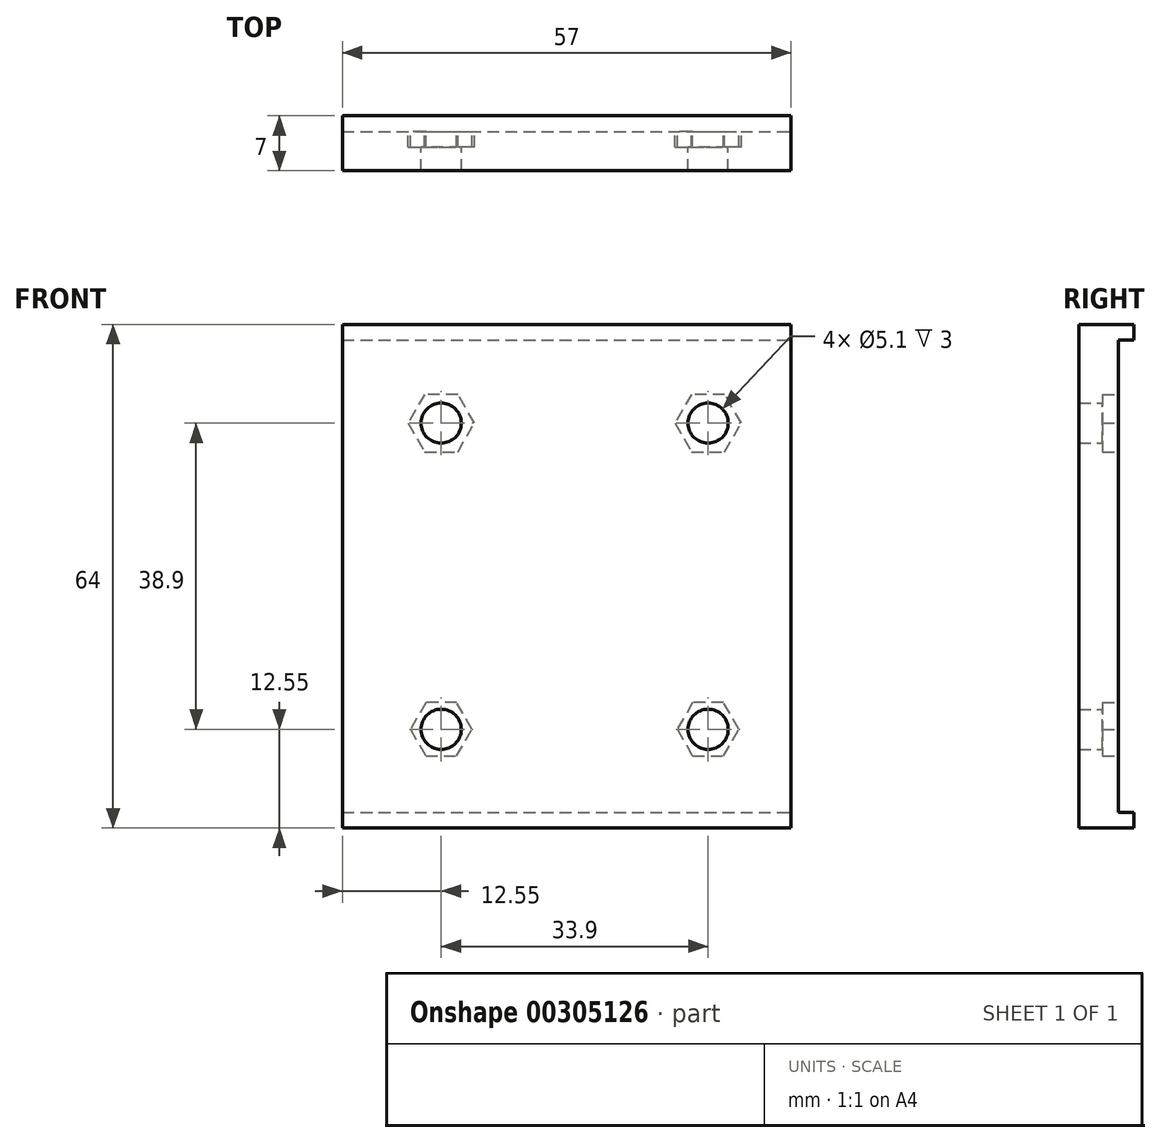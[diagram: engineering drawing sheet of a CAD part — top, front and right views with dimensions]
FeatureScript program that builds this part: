
annotation { "Feature Type Name" : "Feature", "Feature Type Description" : "" }
export const myFeature = defineFeature(function(context is Context, id is Id, definition is map)
    precondition{}
    {
        {
            var Q0;
            Q0=qCreatedBy(makeId("Front.planeOp"),FACE);
            var sketch = newSketch(context, id + "F0", { "sketchPlane" : qUnion([Q0])});
            skLineSegment(sketch, "E0.left", {"start": v(-55, 58.9) * mm, "end": v(-55, -1.1) * mm});
            skLineSegment(sketch, "E0.right", {"start": v(2, 58.9) * mm, "end": v(2, -1.1) * mm});
            skLineSegment(sketch, "E1.0", {"start": v(-55, 58.9) * mm, "end": v(2, 58.9) * mm});
            skLineSegment(sketch, "E2.0", {"start": v(-55, -1.1) * mm, "end": v(2, -1.1) * mm});
            skCircle(sketch, "E3", {"center": v(-42.45, 48.35) * mm, "radius": 2.55 * mm});
            skCircle(sketch, "E4", {"center": v(-8.55, 48.35) * mm, "radius": 2.55 * mm});
            skCircle(sketch, "E5", {"center": v(-42.45, 9.45) * mm, "radius": 2.55 * mm});
            skCircle(sketch, "E6", {"center": v(-8.55, 9.45) * mm, "radius": 2.55 * mm});
            skSolve(sketch);
        }
        {
            var Q0;
            {var subQ0=sQuery(id+"F0.wireOp",EDGE,"E1.0");Q0=makeQuery(id+"F0.imprint","IMPRINT",FACE,{"disambiguationData":[TD([[makeQuery(id+"F0.imprint","IMPRINT",EDGE,{"derivedFrom":subQ0}),-1.0]])]});}
            extrude(context, id + "F1", {"entities" : qUnion([Q0]), "endBound" : BoundingType.SYMMETRIC, "depth" : 5 * mm});
        }
        {
            var Q0;
            Q0=makeQuery(id+"F1.opExtrude","CAP_FACE",FACE,{"disambiguationData":[OSD([sQuery(id+"F0.wireOp",EDGE,"E0.left"),sQuery(id+"F0.wireOp",EDGE,"E0.right"),sQuery(id+"F0.wireOp",EDGE,"E1.0"),sQuery(id+"F0.wireOp",EDGE,"E2.0")])],"isStart":false});
            var sketch = newSketch(context, id + "F2", { "sketchPlane" : qUnion([Q0])});
            skLineSegment(sketch, "E7.0", {"start": v(-55, 60.9) * mm, "end": v(2, 60.9) * mm});
            skLineSegment(sketch, "E8.0", {"start": v(-55, -3.1) * mm, "end": v(2, -3.1) * mm});
            skLineSegment(sketch, "E9", {"start": v(-55, -3.1) * mm, "end": v(-55, -1.1) * mm});
            skLineSegment(sketch, "E10", {"start": v(-55, 60.9) * mm, "end": v(-55, 58.9) * mm});
            skLineSegment(sketch, "E11", {"start": v(2, 60.9) * mm, "end": v(2, 58.9) * mm});
            skLineSegment(sketch, "E12", {"start": v(2, -3.1) * mm, "end": v(2, -1.1) * mm});
            skSolve(sketch);
        }
        {
            var Q0;
            Q0 = qSketchRegion(id + "F2", true);
            var Q1;
            Q1=makeQuery(id+"F2.imprint","IMPRINT",FACE,{"disambiguationData":[TD([[makeQuery(id+"F2.imprint","IMPRINT",EDGE,{"derivedFrom":sQuery(id+"F2.wireOp",EDGE,"E7.0")}),-1.0]])]});
            var Q2;
            Q2=makeQuery(id+"F2.imprint","IMPRINT",FACE,{"disambiguationData":[TD([[makeQuery(id+"F2.imprint","IMPRINT",EDGE,{"derivedFrom":sQuery(id+"F2.wireOp",EDGE,"E8.0")}),1.0]])]});
            extrude(context, id + "F3", {"entities" : qUnion([Q0, Q1, Q2]), "operationType" : NewBodyOperationType.ADD, "oppositeDirection" : true, "depth" : 7 * mm});
        }
        {
            var Q0;
            Q0=makeQuery(id+"F3.opExtrude","SWEPT_FACE",FACE,{"disambiguationData":[OSD([sQuery(id+"F2.wireOp",EDGE,"E7.0")])]});
            var sketch = newSketch(context, id + "F4", { "sketchPlane" : qUnion([Q0])});
            skSolve(sketch);
        }
        {
            var Q0;
            Q0=makeQuery(id+"F1.opExtrude","CAP_FACE",FACE,{"disambiguationData":[OSD([sQuery(id+"F0.wireOp",EDGE,"E0.left"),sQuery(id+"F0.wireOp",EDGE,"E0.right"),sQuery(id+"F0.wireOp",EDGE,"E1.0"),sQuery(id+"F0.wireOp",EDGE,"E2.0"),sQuery(id+"F0.wireOp",EDGE,"E3"),sQuery(id+"F0.wireOp",EDGE,"E4"),sQuery(id+"F0.wireOp",EDGE,"E5"),sQuery(id+"F0.wireOp",EDGE,"E6")])],"isStart":true});
            var sketch = newSketch(context, id + "F5", { "sketchPlane" : qUnion([Q0])});
            skCircle(sketch, "E13.cCircle", {"center": v(42.45, 48.35) * mm, "radius": 3.65 * mm, "construction": true});
            skLineSegment(sketch, "E13.0", {"start": v(44.56, 44.7) * mm, "end": v(40.34, 44.7) * mm});
            skLineSegment(sketch, "E13.1", {"start": v(40.34, 44.7) * mm, "end": v(38.24, 48.35) * mm});
            skLineSegment(sketch, "E13.2", {"start": v(38.24, 48.35) * mm, "end": v(40.34, 52) * mm});
            skLineSegment(sketch, "E13.3", {"start": v(40.34, 52) * mm, "end": v(44.56, 52) * mm});
            skLineSegment(sketch, "E13.4", {"start": v(44.56, 52) * mm, "end": v(46.66, 48.35) * mm});
            skLineSegment(sketch, "E13.5", {"start": v(46.66, 48.35) * mm, "end": v(44.56, 44.7) * mm});
            skPoint(sketch, "E13.0.midPoint", {"position": v(42.45, 44.7) * mm});
            skCircle(sketch, "E14.cCircle", {"center": v(8.55, 48.35) * mm, "radius": 3.65 * mm, "construction": true});
            skLineSegment(sketch, "E14.0", {"start": v(10.66, 44.7) * mm, "end": v(6.44, 44.7) * mm});
            skLineSegment(sketch, "E14.1", {"start": v(6.44, 44.7) * mm, "end": v(4.34, 48.35) * mm});
            skLineSegment(sketch, "E14.2", {"start": v(4.34, 48.35) * mm, "end": v(6.44, 52) * mm});
            skLineSegment(sketch, "E14.3", {"start": v(6.44, 52) * mm, "end": v(10.66, 52) * mm});
            skLineSegment(sketch, "E14.4", {"start": v(10.66, 52) * mm, "end": v(12.76, 48.35) * mm});
            skLineSegment(sketch, "E14.5", {"start": v(12.76, 48.35) * mm, "end": v(10.66, 44.7) * mm});
            skPoint(sketch, "E14.0.midPoint", {"position": v(8.55, 44.7) * mm});
            skCircle(sketch, "E15.cCircle", {"center": v(8.55, 9.45) * mm, "radius": 3.4 * mm, "construction": true});
            skLineSegment(sketch, "E15.0", {"start": v(10.5, 6.06) * mm, "end": v(6.6, 6.06) * mm});
            skLineSegment(sketch, "E15.1", {"start": v(6.6, 6.06) * mm, "end": v(4.63, 9.45) * mm});
            skLineSegment(sketch, "E15.2", {"start": v(4.63, 9.45) * mm, "end": v(6.6, 12.84) * mm});
            skLineSegment(sketch, "E15.3", {"start": v(6.6, 12.84) * mm, "end": v(10.5, 12.84) * mm});
            skLineSegment(sketch, "E15.4", {"start": v(10.5, 12.84) * mm, "end": v(12.47, 9.45) * mm});
            skLineSegment(sketch, "E15.5", {"start": v(12.47, 9.45) * mm, "end": v(10.5, 6.06) * mm});
            skPoint(sketch, "E15.0.midPoint", {"position": v(8.55, 6.06) * mm});
            skCircle(sketch, "E16.cCircle", {"center": v(42.45, 9.45) * mm, "radius": 3.4 * mm, "construction": true});
            skLineSegment(sketch, "E16.0", {"start": v(44.4, 6.06) * mm, "end": v(40.5, 6.06) * mm});
            skLineSegment(sketch, "E16.1", {"start": v(40.5, 6.06) * mm, "end": v(38.53, 9.45) * mm});
            skLineSegment(sketch, "E16.2", {"start": v(38.53, 9.45) * mm, "end": v(40.5, 12.84) * mm});
            skLineSegment(sketch, "E16.3", {"start": v(40.5, 12.84) * mm, "end": v(44.4, 12.84) * mm});
            skLineSegment(sketch, "E16.4", {"start": v(44.4, 12.84) * mm, "end": v(46.37, 9.45) * mm});
            skLineSegment(sketch, "E16.5", {"start": v(46.37, 9.45) * mm, "end": v(44.4, 6.06) * mm});
            skPoint(sketch, "E16.0.midPoint", {"position": v(42.45, 6.06) * mm});
            skSolve(sketch);
        }
        {
            var Q0;
            Q0=makeQuery(id+"F5.imprint","IMPRINT",FACE,{"disambiguationData":[TD([[makeQuery(id+"F5.imprint","IMPRINT",EDGE,{"derivedFrom":sQuery(id+"F5.wireOp",EDGE,"E16.0")}),-1.0]])]});
            var Q1;
            Q1=makeQuery(id+"F5.imprint","IMPRINT",FACE,{"disambiguationData":[TD([[makeQuery(id+"F5.imprint","IMPRINT",EDGE,{"derivedFrom":sQuery(id+"F5.wireOp",EDGE,"E15.0")}),-1.0]])]});
            var Q2;
            Q2=makeQuery(id+"F5.imprint","IMPRINT",FACE,{"disambiguationData":[TD([[makeQuery(id+"F5.imprint","IMPRINT",EDGE,{"derivedFrom":sQuery(id+"F5.wireOp",EDGE,"E14.0")}),-1.0]])]});
            var Q3;
            Q3=makeQuery(id+"F5.imprint","IMPRINT",FACE,{"disambiguationData":[TD([[makeQuery(id+"F5.imprint","IMPRINT",EDGE,{"derivedFrom":sQuery(id+"F5.wireOp",EDGE,"E13.0")}),-1.0]])]});
            extrude(context, id + "F6", {"entities" : qUnion([Q0, Q1, Q2, Q3]), "operationType" : NewBodyOperationType.REMOVE, "oppositeDirection" : true, "depth" : 2 * mm});
        }
    });
